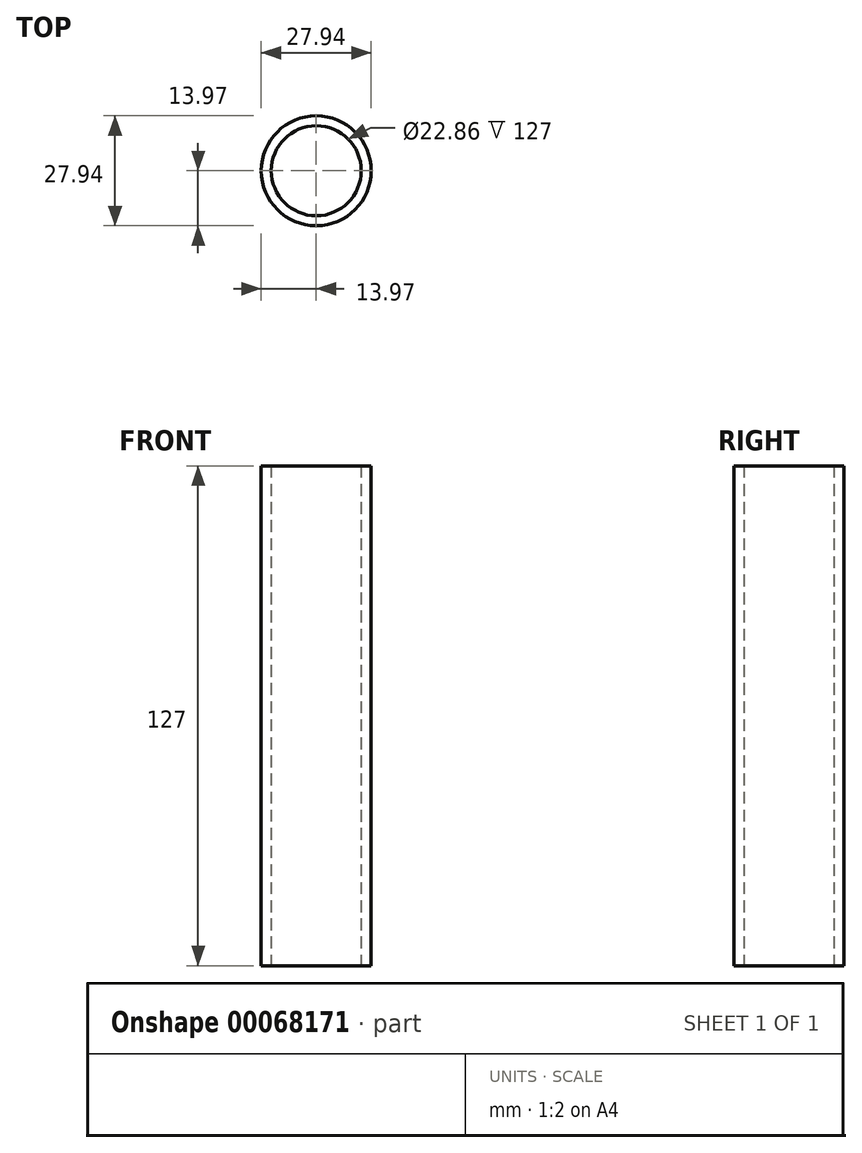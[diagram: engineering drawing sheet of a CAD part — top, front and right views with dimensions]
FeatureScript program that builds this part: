
annotation { "Feature Type Name" : "Feature", "Feature Type Description" : "" }
export const myFeature = defineFeature(function(context is Context, id is Id, definition is map)
    precondition{}
    {
        {
            var Q0;
            Q0=qCreatedBy(makeId("Top.planeOp"),FACE);
            var sketch = newSketch(context, id + "F0", { "sketchPlane" : qUnion([Q0])});
            skCircle(sketch, "E0", {"center": v(0, 0) * mm, "radius": 11.43 * mm});
            skCircle(sketch, "E1", {"center": v(0, 0) * mm, "radius": 13.97 * mm});
            skSolve(sketch);
        }
        {
            var Q0;
            Q0=makeQuery(id+"F0.imprint","IMPRINT",FACE,{"disambiguationData":[TD([[makeQuery(id+"F0.imprint","IMPRINT",EDGE,{"derivedFrom":sQuery(id+"F0.wireOp",EDGE,"E0")}),-1.0]])]});
            extrude(context, id + "F1", {"entities" : qUnion([Q0]), "depth" : 127 * mm});
        }
    });
